# Revit family: Bicycle-Racks_BR-Square_Huntco_BRS3
name_source: partatom
category: Site
units: mm (PartAtom-declared; Revit-internal decimal feet)

## family parameters
Cut with Voids When Loaded = No
Host = Face
Part Type = Normal
Round Connector Dimension = Use Diameter
Shared = No

## types (1)
- Bicycle-Racks_BR-Square_Huntco_BRS3
    Assembly Code = G2040500
    Capacity = Bike Capacity as Specified
    Construction Details = http://www.arcat.com
    Covered Flange = No
    Default Elevation = 4' - 0"
    Description = Huntco Product as Specified
    Embedded Mounted = No
    Expected Lifespan (Years) = 0
    Exposed Flange = Yes
    Flange Mounted = Yes
    Freestanding = No
    Green Building-LEED = http://www.arcat.com
    Keynote = 02871
    Maintenance Schedule (Months) = 0
    Manufacturer = Huntco Supply LLC
    Manufacturer Fax = 503-274-2055
    Manufacturer Website = http://www.huntco.com
    Material Finish = Metal - Steel - Huntco - Stainless
    Model = As Specified
    Pipe Diameter = 0' - 2"
    Product Data = http://www.arcat.com
    Revision = R1_11_2012
    Send Message = http://www.arcat.com
    Specification = http://www.arcat.com
    URL = http://www.huntco.com
    Unit Height = 3' - 0"
    Unit Weight = 0
    Unit Width = 1' - 2 3/8"
    Warranty Duration (Years) = 0
    extralength = 0' - 0"
    flangeheight = 0' - 0 1/2"
    flangevisible = Yes
    holedepth = 0' - 4"
    holediameter = 0' - 0 1/2"

## geometry (parser evidence)
native form markers: Sweep x2
no freeform markers — native parametric forms only
